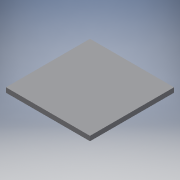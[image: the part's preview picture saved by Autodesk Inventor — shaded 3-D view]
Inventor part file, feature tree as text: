
AUTODESK INVENTOR PART (.ipt)
format: ipt  version: 2018.3 (Build 223284000, 284)  size: 82,432 bytes
history: native  units: mm
features: extrude x1, sketch x1
ambient origin geometry x8: Origin, YZ Plane, XZ Plane, XY Plane, X Axis, Y Axis, Z Axis, Center Point
bodies: Solid1 (feature_tree)
feature tree (2):
  extrude  "Extrusion1"  Depth=36.0mm
  sketch  "Sketch1"  dims[d0=36.0mm d1=36.0mm d2=2.0mm d3=0.0mm]
